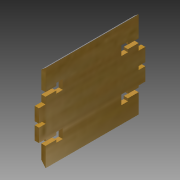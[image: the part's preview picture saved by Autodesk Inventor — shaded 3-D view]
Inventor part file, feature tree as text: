
AUTODESK INVENTOR PART (.ipt)
format: ipt  version: 2014 (Build 180170000, 170)  size: 218,624 bytes
history: native  units: mm
features: extrude x8, sketch x3
ambient origin geometry x8: Origin, YZ Plane, XZ Plane, XY Plane, X Axis, Y Axis, Z Axis, Center Point
bodies: Body1 (feature_tree)
feature tree (11):
  sketch  "Sketch3"  dims[d17=70.0mm d18=0.0mm d23=16.0mm]
  extrude  "Extrusion4"  Depth=70.0mm
  sketch  "Sketch4"  dims[d24=32.0mm d25=16.0mm]
  extrude  "Extrusion5"  Depth=32.0mm
  extrude  "Extrusion6"  Depth=8.0mm
  extrude  "Extrusion7"  Depth=2.0mm
  extrude  "Extrusion8"  Depth=5.0mm
  sketch  "Sketch6"  dims[d26=1.5mm d27=8.0mm d28=2.0mm d29=5.0mm d30=7.0mm d31=2.0mm d32=1.5mm d33=1.5mm d34=1.5mm d35=1.5mm d36=8.0mm d37=2.0mm d38=7.0mm d39=70.0mm d40=8.0mm d41=2.0mm d42=5.0mm d43=7.0mm d44=5.0mm d45=1.5mm d46=8.0mm d47=2.0mm d48=3.2mm d49=0.0mm d50=3.2mm d51=0.0mm d52=3.2mm d53=0.0mm d54=3.2mm d55=0.0mm d63=3.123mm d65=64.0mm d75=15.0mm d76=10.0mm d77=20.0mm d78=10.0mm d80=15.0mm d81=10.0mm d84=5.0mm d85=0.0mm d86=20.0mm d87=10.0mm d88=5.0mm d89=0.0mm d90=16.0mm d91=16.0mm d92=2.904334mm d93=6.498808mm d94=1.0mm d95=6.749188mm d96=1.3mm d97=70.0mm d98=0.0mm]
  extrude  "Extrusion13"  Depth=7.0mm
  extrude  "Extrusion14"  Depth=2.0mm
  extrude  "Extrusion15"  Depth=70.0mm
